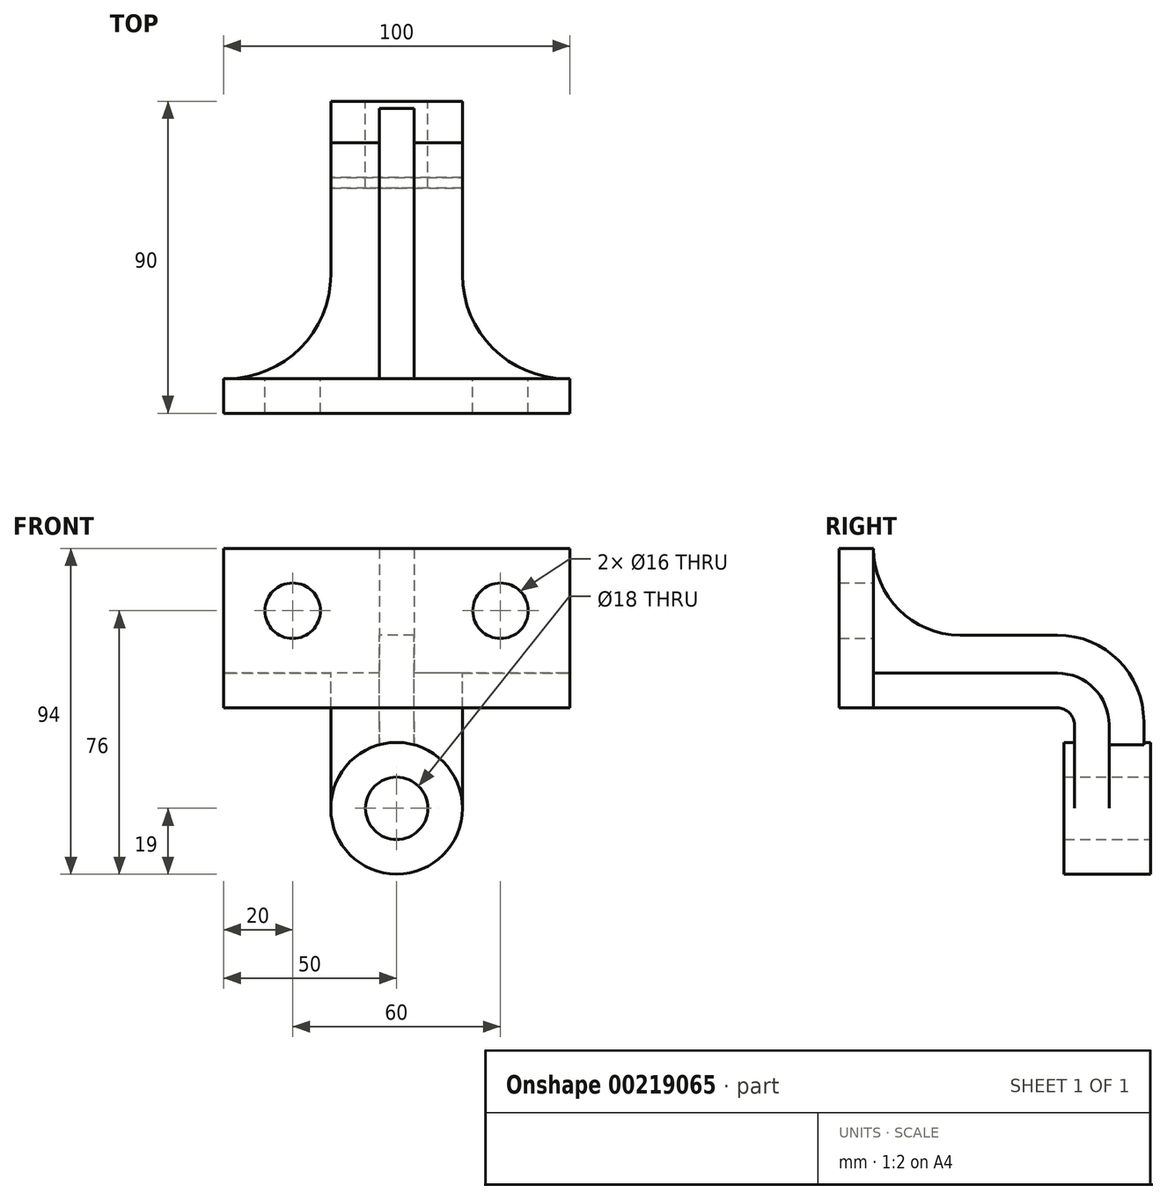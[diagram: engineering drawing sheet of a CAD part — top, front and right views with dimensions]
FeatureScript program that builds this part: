
annotation { "Feature Type Name" : "Feature", "Feature Type Description" : "" }
export const myFeature = defineFeature(function(context is Context, id is Id, definition is map)
    precondition{}
    {
        {
            var Q0;
            Q0=qCreatedBy(makeId("Right.planeOp"),FACE);
            var sketch = newSketch(context, id + "F0", { "sketchPlane" : qUnion([Q0])});
            skLineSegment(sketch, "E0.bottom", {"start": v(0, 46) * mm, "end": v(10, 46) * mm});
            skLineSegment(sketch, "E0.top", {"start": v(0, 0) * mm, "end": v(10, 0) * mm});
            skLineSegment(sketch, "E0.left", {"start": v(0, 46) * mm, "end": v(0, 0) * mm});
            skLineSegment(sketch, "E0.right", {"start": v(10, 46) * mm, "end": v(10, 0) * mm});
            skLineSegment(sketch, "E1.bottom", {"start": v(10, 0) * mm, "end": v(68, 0) * mm});
            skLineSegment(sketch, "E1.top", {"start": v(10, 10) * mm, "end": v(78, 10) * mm});
            skLineSegment(sketch, "E1.left", {"start": v(10, 0) * mm, "end": v(10, 10) * mm});
            skLineSegment(sketch, "E1.right", {"start": v(78, 0) * mm, "end": v(78, 10) * mm});
            skLineSegment(sketch, "E2.top", {"start": v(78, -29) * mm, "end": v(68, -29) * mm});
            skLineSegment(sketch, "E2.left", {"start": v(78, 0) * mm, "end": v(78, -29) * mm});
            skLineSegment(sketch, "E2.right", {"start": v(68, 0) * mm, "end": v(68, -29) * mm});
            skSolve(sketch);
        }
        {
            var Q0;
            Q0=makeQuery(id+"F0.imprint","IMPRINT",FACE,{"disambiguationData":[TD([[makeQuery(id+"F0.imprint","IMPRINT",EDGE,{"derivedFrom":sQuery(id+"F0.wireOp",EDGE,"E0.bottom")}),-1.0]])]});
            extrude(context, id + "F1", {"entities" : qUnion([Q0]), "endBound" : BoundingType.SYMMETRIC, "depth" : 100 * mm});
        }
        {
            var Q0;
            Q0=makeQuery(id+"F0.imprint","IMPRINT",FACE,{"disambiguationData":[TD([[makeQuery(id+"F0.imprint","IMPRINT",EDGE,{"derivedFrom":sQuery(id+"F0.wireOp",EDGE,"E1.bottom")}),1.0]])]});
            var Q1;
            Q1=makeQuery(id+"F1.opExtrude","CAP_FACE",FACE,{"disambiguationData":[OSD([sQuery(id+"F0.wireOp",EDGE,"E0.bottom"),sQuery(id+"F0.wireOp",EDGE,"E0.top"),sQuery(id+"F0.wireOp",EDGE,"E0.left"),sQuery(id+"F0.wireOp",EDGE,"E0.right"),sQuery(id+"F0.wireOp",EDGE,"E1.left")])],"isStart":false});
            extrude(context, id + "F2", {"entities" : qUnion([Q0]), "operationType" : NewBodyOperationType.ADD, "endBound" : BoundingType.SYMMETRIC, "endBoundEntityFace" : qUnion([Q1]), "depth" : 100 * mm});
        }
        {
            var Q0;
            Q0=qCreatedBy(makeId("Right.planeOp"),FACE);
            var sketch = newSketch(context, id + "F3", { "sketchPlane" : qUnion([Q0])});
            skLineSegment(sketch, "E3.0", {"start": v(10, 46) * mm, "end": v(10, 10) * mm});
            skLineSegment(sketch, "E4.0", {"start": v(10, 10) * mm, "end": v(78, 10) * mm});
            skLineSegment(sketch, "E5.top", {"start": v(10, 46) * mm, "end": v(78, 46) * mm});
            skLineSegment(sketch, "E5.left", {"start": v(10, 10) * mm, "end": v(10, 46) * mm});
            skPoint(sketch, "E6.orphan", {"position": v(10, 46) * mm});
            skPoint(sketch, "E7.orphan", {"position": v(10, 0) * mm});
            skArc(sketch, "E8", {"start": v(10, 46) * mm, "mid": v(17.32, 28.32) * mm, "end": v(35, 21) * mm});
            skLineSegment(sketch, "E9", {"start": v(35, 21) * mm, "end": v(78, 21) * mm});
            skLineSegment(sketch, "E10", {"start": v(88, 46) * mm, "end": v(88, 10) * mm});
            skLineSegment(sketch, "E11", {"start": v(78, 10) * mm, "end": v(88, 10) * mm});
            skLineSegment(sketch, "E12", {"start": v(88, 46) * mm, "end": v(78, 46) * mm});
            skLineSegment(sketch, "E13", {"start": v(78, 21) * mm, "end": v(88, 21) * mm});
            skLineSegment(sketch, "E14.0", {"start": v(78, 0) * mm, "end": v(78, -26) * mm});
            skLineSegment(sketch, "E15.0", {"start": v(78, 0) * mm, "end": v(78, 10) * mm});
            skLineSegment(sketch, "E16.MirrorCS", {"start": v(88, -26) * mm, "end": v(88, 10) * mm});
            skLineSegment(sketch, "E17.MirrorCS", {"start": v(88, -26) * mm, "end": v(78, -26) * mm});
            skPoint(sketch, "E18.orphan", {"position": v(78, -29) * mm});
            skSolve(sketch);
        }
        {
            var Q0;
            Q0=makeQuery(id+"F3.imprint","IMPRINT",FACE,{"disambiguationData":[TD([[makeQuery(id+"F3.imprint","IMPRINT",EDGE,{"derivedFrom":sQuery(id+"F3.wireOp",EDGE,"E4.0")}),1.0]])]});
            var Q1;
            Q1=makeQuery(id+"F3.imprint","IMPRINT",FACE,{"disambiguationData":[TD([[makeQuery(id+"F3.imprint","IMPRINT",EDGE,{"derivedFrom":sQuery(id+"F3.wireOp",EDGE,"E11")}),-1.0]])]});
            extrude(context, id + "F4", {"entities" : qUnion([Q0, Q1]), "operationType" : NewBodyOperationType.ADD, "endBound" : BoundingType.SYMMETRIC, "depth" : 10 * mm});
        }
        {
            var Q0;
            {var subQ3=sQuery(id+"F0.wireOp",EDGE,"E1.left");var subQ4=sQuery(id+"F0.wireOp",EDGE,"E1.top");var subQ5=sQuery(id+"F0.wireOp",EDGE,"E0.right");Q0=makeQuery(id+"F4.boolean.opBoolean","SPLIT",FACE,{"disambiguationData":[TD([makeQuery(id+"F1.opExtrude","CAP_FACE",FACE,{"disambiguationData":[OSD([sQuery(id+"F0.wireOp",EDGE,"E0.bottom"),sQuery(id+"F0.wireOp",EDGE,"E0.top"),sQuery(id+"F0.wireOp",EDGE,"E0.left"),subQ5,subQ3])],"isStart":false})])],"derivedFrom":makeQuery(id+"F2.opExtrude","SWEPT_FACE",FACE,{"disambiguationData":[OSD([subQ4])]})});}
            var sketch = newSketch(context, id + "F5", { "sketchPlane" : qUnion([Q0])});
            skArc(sketch, "E19", {"start": v(19, 40) * mm, "mid": v(28.14, 18.44) * mm, "end": v(50, 10.02) * mm});
            skLineSegment(sketch, "E20", {"start": v(19, 40) * mm, "end": v(19, 78) * mm});
            skLineSegment(sketch, "E21.0", {"start": v(50, 10) * mm, "end": v(50, 78) * mm});
            skLineSegment(sketch, "E22.0", {"start": v(50, 78) * mm, "end": v(19, 78) * mm});
            skPoint(sketch, "E23.orphan", {"position": v(5, 78) * mm});
            skLineSegment(sketch, "E24.MirrorCS", {"start": v(-19, 40) * mm, "end": v(-19, 78) * mm});
            skArc(sketch, "E25.MirrorCS", {"start": v(-19, 40) * mm, "mid": v(-28.14, 18.44) * mm, "end": v(-50, 10.02) * mm});
            skLineSegment(sketch, "E26.MirrorCS", {"start": v(-50, 10) * mm, "end": v(-50, 78) * mm});
            skLineSegment(sketch, "E27.MirrorCS", {"start": v(-50, 78) * mm, "end": v(-19, 78) * mm});
            skSolve(sketch);
        }
        {
            var Q0;
            {var subQ4=sQuery(id+"F5.wireOp",EDGE,"E20");Q0=makeQuery(id+"F5.imprint","IMPRINT",FACE,{"disambiguationData":[TD([[makeQuery(id+"F5.imprint","IMPRINT",EDGE,{"derivedFrom":subQ4}),-1.0]])]});}
            var Q1;
            Q1=makeQuery(id+"F5.imprint","IMPRINT",FACE,{"disambiguationData":[TD([[makeQuery(id+"F5.imprint","IMPRINT",EDGE,{"derivedFrom":sQuery(id+"F5.wireOp",EDGE,"E24.MirrorCS")}),1.0]])]});
            extrude(context, id + "F6", {"entities" : qUnion([Q0, Q1]), "operationType" : NewBodyOperationType.REMOVE, "endBound" : BoundingType.THROUGH_ALL, "oppositeDirection" : true, "depth" : 25 * mm});
        }
        {
            var Q0;
            Q0=makeQuery(id+"F2.opExtrude","SWEPT_EDGE",EDGE,{"disambiguationData":[OSD([sQuery(id+"F0.wireOp",EDGE,"E1.bottom"),sQuery(id+"F0.wireOp",EDGE,"E2.right")])]});
            fillet(context, id + "F7", {"entities" : qUnion([Q0]), "radius" : 5 * mm, "tangentPropagation" : true, "allowEdgeOverflow" : false});
        }
        {
            var Q0;
            Q0=makeQuery(id+"F4.opExtrude","SWEPT_EDGE",EDGE,{"disambiguationData":[OSD([sQuery(id+"F3.wireOp",EDGE,"E10"),sQuery(id+"F3.wireOp",EDGE,"E13")])]});
            fillet(context, id + "F8", {"entities" : qUnion([Q0]), "radius" : 25 * mm, "tangentPropagation" : true, "allowEdgeOverflow" : false});
        }
        {
            var Q0;
            {var subQ0=sQuery(id+"F0.wireOp",EDGE,"E2.left");var subQ1=sQuery(id+"F0.wireOp",EDGE,"E1.right");var subQ2=sQuery(id+"F3.wireOp",EDGE,"E11");var subQ3=sQuery(id+"F3.wireOp",EDGE,"E4.0");var subQ4=sQuery(id+"F0.wireOp",EDGE,"E1.top");var subQ5=sQuery(id+"F0.wireOp",EDGE,"E1.left");Q0=makeQuery(id+"F4.boolean.opBoolean","SPLIT",EDGE,{"disambiguationData":[TD([makeQuery(id+"F1.opExtrude","CAP_FACE",FACE,{"disambiguationData":[OSD([sQuery(id+"F0.wireOp",EDGE,"E0.bottom"),sQuery(id+"F0.wireOp",EDGE,"E0.top"),sQuery(id+"F0.wireOp",EDGE,"E0.left"),sQuery(id+"F0.wireOp",EDGE,"E0.right"),subQ5])],"isStart":false}),makeQuery(id+"F2.opExtrude","CAP_FACE",FACE,{"disambiguationData":[OSD([sQuery(id+"F0.wireOp",EDGE,"E1.bottom"),subQ4,subQ5,subQ1,sQuery(id+"F0.wireOp",EDGE,"E2.top"),subQ0,sQuery(id+"F0.wireOp",EDGE,"E2.right")])],"isStart":false}),makeQuery(id+"F2.opExtrude","SWEPT_FACE",FACE,{"disambiguationData":[OSD([subQ4])]}),makeQuery(id+"F2.opExtrude","SWEPT_FACE",FACE,{"disambiguationData":[OSD([subQ1,subQ0])]}),makeQuery(id+"F4.opExtrude","CAP_FACE",FACE,{"disambiguationData":[OSD([subQ3,sQuery(id+"F3.wireOp",EDGE,"E5.left"),sQuery(id+"F3.wireOp",EDGE,"E8"),sQuery(id+"F3.wireOp",EDGE,"E9"),sQuery(id+"F3.wireOp",EDGE,"E10"),subQ2,sQuery(id+"F3.wireOp",EDGE,"E13")])],"isStart":false}),makeQuery(id+"F4.opExtrude","SWEPT_FACE",FACE,{"disambiguationData":[OSD([subQ3,subQ2])]})])],"derivedFrom":makeQuery(id+"F2.opExtrude","SWEPT_EDGE",EDGE,{"disambiguationData":[OSD([subQ4,subQ1])]})});}
            var Q1;
            {var subQ0=sQuery(id+"F0.wireOp",EDGE,"E1.top");var subQ1=sQuery(id+"F3.wireOp",EDGE,"E11");var subQ2=sQuery(id+"F3.wireOp",EDGE,"E4.0");var subQ3=sQuery(id+"F0.wireOp",EDGE,"E2.left");var subQ4=sQuery(id+"F0.wireOp",EDGE,"E1.right");var subQ5=sQuery(id+"F0.wireOp",EDGE,"E1.left");Q1=makeQuery(id+"F4.boolean.opBoolean","SPLIT",EDGE,{"disambiguationData":[TD([makeQuery(id+"F1.opExtrude","CAP_FACE",FACE,{"disambiguationData":[OSD([sQuery(id+"F0.wireOp",EDGE,"E0.bottom"),sQuery(id+"F0.wireOp",EDGE,"E0.top"),sQuery(id+"F0.wireOp",EDGE,"E0.left"),sQuery(id+"F0.wireOp",EDGE,"E0.right"),subQ5])],"isStart":true}),makeQuery(id+"F2.opExtrude","CAP_FACE",FACE,{"disambiguationData":[OSD([sQuery(id+"F0.wireOp",EDGE,"E1.bottom"),subQ0,subQ5,subQ4,sQuery(id+"F0.wireOp",EDGE,"E2.top"),subQ3,sQuery(id+"F0.wireOp",EDGE,"E2.right")])],"isStart":true}),makeQuery(id+"F2.opExtrude","SWEPT_FACE",FACE,{"disambiguationData":[OSD([subQ0])]}),makeQuery(id+"F2.opExtrude","SWEPT_FACE",FACE,{"disambiguationData":[OSD([subQ4,subQ3])]}),makeQuery(id+"F4.opExtrude","CAP_FACE",FACE,{"disambiguationData":[OSD([subQ2,sQuery(id+"F3.wireOp",EDGE,"E5.left"),sQuery(id+"F3.wireOp",EDGE,"E8"),sQuery(id+"F3.wireOp",EDGE,"E9"),sQuery(id+"F3.wireOp",EDGE,"E10"),subQ1,sQuery(id+"F3.wireOp",EDGE,"E13")])],"isStart":true}),makeQuery(id+"F4.opExtrude","SWEPT_FACE",FACE,{"disambiguationData":[OSD([subQ2,subQ1])]})])],"derivedFrom":makeQuery(id+"F2.opExtrude","SWEPT_EDGE",EDGE,{"disambiguationData":[OSD([subQ0,subQ4])]})});}
            fillet(context, id + "F9", {"entities" : qUnion([Q0, Q1]), "radius" : 15 * mm, "tangentPropagation" : true, "allowEdgeOverflow" : false});
        }
        {
            var Q0;
            Q0=qCreatedBy(makeId("Front.planeOp"),FACE);
            cPlane(context, id + "F10", {"entities" : qUnion([Q0]), "cplaneType" : CPlaneType.OFFSET, "offset" : 90 * mm, "oppositeDirection" : true, "width" : 150 * mm, "height" : 150 * mm});
        }
        {
            var Q0;
            Q0=qCreatedBy(id+"F10.planeOp",FACE);
            var sketch = newSketch(context, id + "F11", { "sketchPlane" : qUnion([Q0])});
            skPoint(sketch, "E28.0", {"position": v(0, -29) * mm});
            skCircle(sketch, "E29", {"center": v(0, -29) * mm, "radius": 19 * mm});
            skCircle(sketch, "E30", {"center": v(0, -29) * mm, "radius": 9 * mm});
            skSolve(sketch);
        }
        {
            var Q0;
            Q0=makeQuery(id+"F11.imprint","IMPRINT",FACE,{"disambiguationData":[TD([[makeQuery(id+"F11.imprint","IMPRINT",EDGE,{"derivedFrom":sQuery(id+"F11.wireOp",EDGE,"E29")}),1.0]])]});
            extrude(context, id + "F12", {"entities" : qUnion([Q0]), "operationType" : NewBodyOperationType.ADD, "depth" : 25 * mm});
        }
        {
            var Q0;
            Q0=makeQuery(id+"F12.opExtrude","CAP_FACE",FACE,{"disambiguationData":[OSD([sQuery(id+"F11.wireOp",EDGE,"E29"),sQuery(id+"F11.wireOp",EDGE,"E30")])],"isStart":true});
            var sketch = newSketch(context, id + "F13", { "sketchPlane" : qUnion([Q0])});
            skCircle(sketch, "E31.0", {"center": v(0, -29) * mm, "radius": 9 * mm});
            skSolve(sketch);
        }
        {
            var Q0;
            Q0 = qSketchRegion(id + "F13", true);
            extrude(context, id + "F14", {"entities" : qUnion([Q0]), "operationType" : NewBodyOperationType.REMOVE, "oppositeDirection" : true, "depth" : 25 * mm});
        }
        {
            var Q0;
            {var subQ1=sQuery(id+"F0.wireOp",EDGE,"E1.left");var subQ2=sQuery(id+"F0.wireOp",EDGE,"E0.right");var subQ3=sQuery(id+"F0.wireOp",EDGE,"E0.bottom");Q0=makeQuery(id+"F4.boolean.opBoolean","SPLIT",FACE,{"disambiguationData":[TD([makeQuery(id+"F1.opExtrude","CAP_FACE",FACE,{"disambiguationData":[OSD([subQ3,sQuery(id+"F0.wireOp",EDGE,"E0.top"),sQuery(id+"F0.wireOp",EDGE,"E0.left"),subQ2,subQ1])],"isStart":false})])],"derivedFrom":makeQuery(id+"F1.opExtrude","SWEPT_FACE",FACE,{"disambiguationData":[OSD([subQ2,subQ1])]})});}
            var sketch = newSketch(context, id + "F15", { "sketchPlane" : qUnion([Q0])});
            skCircle(sketch, "E32", {"center": v(-30, 28) * mm, "radius": 8 * mm});
            skCircle(sketch, "E33.MirrorC", {"center": v(30, 28) * mm, "radius": 8 * mm});
            skSolve(sketch);
        }
        {
            var Q0;
            Q0 = qSketchRegion(id + "F15", true);
            extrude(context, id + "F16", {"entities" : qUnion([Q0]), "operationType" : NewBodyOperationType.REMOVE, "oppositeDirection" : true, "depth" : 25 * mm});
        }
    });
